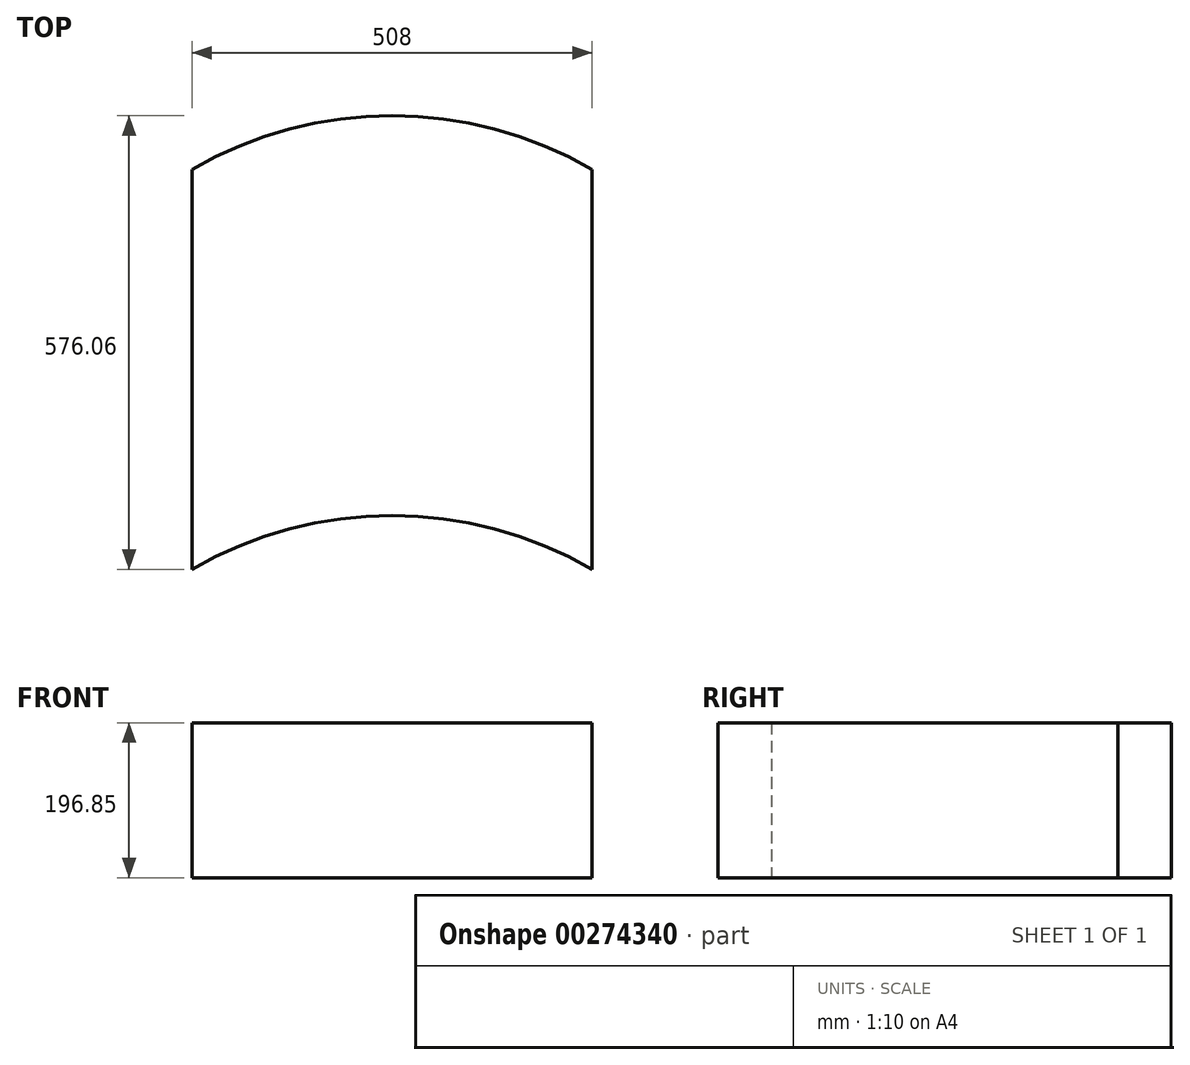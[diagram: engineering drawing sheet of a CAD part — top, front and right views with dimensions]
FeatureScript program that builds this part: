
annotation { "Feature Type Name" : "Feature", "Feature Type Description" : "" }
export const myFeature = defineFeature(function(context is Context, id is Id, definition is map)
    precondition{}
    {
        {
            var Q0;
            Q0=qCreatedBy(makeId("Top.planeOp"),FACE);
            var sketch = newSketch(context, id + "F0", { "sketchPlane" : qUnion([Q0])});
            skLineSegment(sketch, "E0", {"start": v(-51.08, 0) * mm, "end": v(456.92, 0) * mm});
            skLineSegment(sketch, "E1", {"start": v(-51.08, 0) * mm, "end": v(-51.08, 508) * mm});
            skLineSegment(sketch, "E2", {"start": v(456.92, 0) * mm, "end": v(456.92, 508) * mm});
            skArc(sketch, "E3", {"start": v(456.92, 0) * mm, "mid": v(202.92, 68.06) * mm, "end": v(-51.08, 0) * mm});
            skArc(sketch, "E4", {"start": v(456.92, 508) * mm, "mid": v(202.92, 576.06) * mm, "end": v(-51.08, 508) * mm});
            skSolve(sketch);
        }
        {
            var Q0;
            Q0=makeQuery(id+"F0.imprint","IMPRINT",FACE,{"disambiguationData":[TD([[makeQuery(id+"F0.imprint","IMPRINT",EDGE,{"derivedFrom":sQuery(id+"F0.wireOp",EDGE,"E1")}),-1.0]])]});
            extrude(context, id + "F1", {"entities" : qUnion([Q0]), "depth" : 196.85 * mm});
        }
    });
